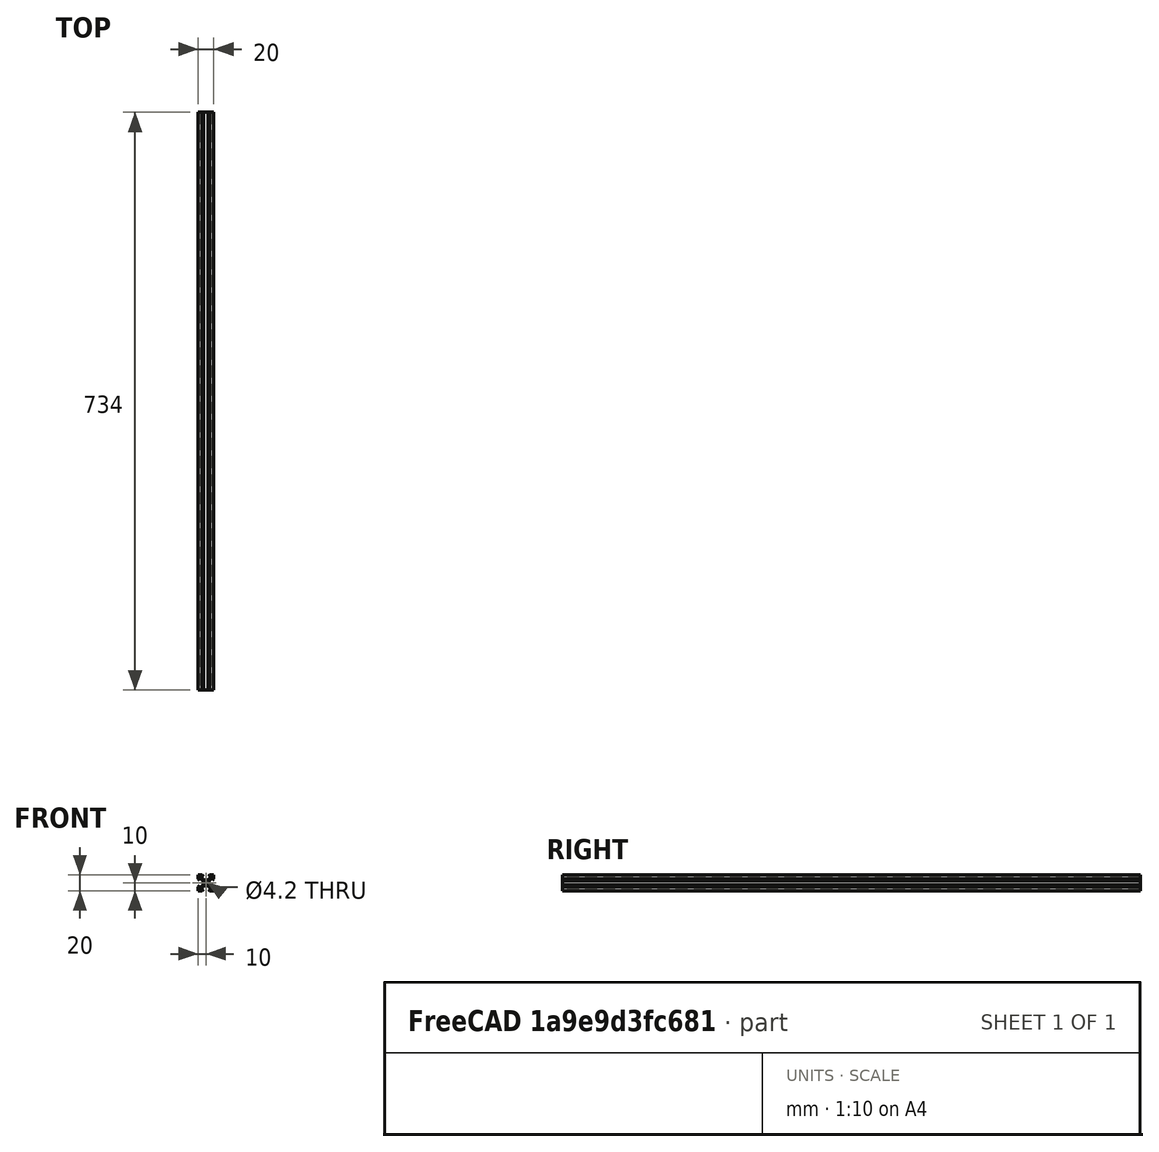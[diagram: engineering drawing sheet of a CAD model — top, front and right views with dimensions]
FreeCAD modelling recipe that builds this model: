
FCSTD DOCUMENT  (FreeCAD 0.20R29177 (Git))
Label: Vlot long
License: All rights reserved
LicenseURL: http://en.wikipedia.org/wiki/All_rights_reserved
objects: Sketcher::SketchObject×1, PartDesign::Pad×1, PartDesign::Body×1
note: 4 computed .brp shape members not serialized (recipe doc carries the construction recipe); baked Part::Feature solids carry a one-line shape summary decoded from their .brp

FEATURE [Sketcher::SketchObject] Sketch
  FullyConstrained = true
  MapMode = 5
  Placement = pos=(0,0,0) rot=(1,0,0;1.5708rad)
  Support = -> [XZ_Plane]
  sketch-geometry (43):
    g0: LineSegment StartX=0 StartY=0 StartZ=0 EndX=5.05 EndY=0 EndZ=0
    g1: LineSegment StartX=20 StartY=20 StartZ=0 EndX=14.95 EndY=20 EndZ=0
    g2: LineSegment StartX=0 StartY=20 StartZ=0 EndX=0 EndY=14.95 EndZ=0
    g3: LineSegment StartX=5.05 StartY=20 StartZ=0 EndX=6.9 EndY=18.15 EndZ=0
    g4: LineSegment StartX=6.9 StartY=18.15 StartZ=0 EndX=2.91066 EndY=18.15 EndZ=0
    g5: LineSegment StartX=2.91066 StartY=18.15 StartZ=0 EndX=7.16066 EndY=13.9 EndZ=0
    g6: LineSegment StartX=7.16066 StartY=13.9 StartZ=0 EndX=12.8393 EndY=13.9 EndZ=0
    g7: LineSegment StartX=12.8393 StartY=13.9 StartZ=0 EndX=17.0893 EndY=18.15 EndZ=0
    g8: LineSegment StartX=17.0893 StartY=18.15 StartZ=0 EndX=13.1 EndY=18.15 EndZ=0
    g9: LineSegment StartX=13.1 StartY=18.15 StartZ=0 EndX=14.95 EndY=20 EndZ=0
    g10: LineSegment StartX=0 StartY=20 StartZ=0 EndX=2.91066 EndY=18.15 EndZ=0
    g11: LineSegment StartX=17.0893 StartY=18.15 StartZ=0 EndX=20 EndY=20 EndZ=0
    g12: LineSegment StartX=0 StartY=20 StartZ=0 EndX=20 EndY=0 EndZ=0
    g13: LineSegment StartX=5.05 StartY=20 StartZ=0 EndX=0 EndY=20 EndZ=0
    g14: LineSegment StartX=0 StartY=20 StartZ=0 EndX=20 EndY=20 EndZ=0
    g15: LineSegment StartX=20 StartY=14.95 StartZ=0 EndX=18.15 EndY=13.1 EndZ=0
    g16: LineSegment StartX=18.15 StartY=13.1 StartZ=0 EndX=18.15 EndY=17.0893 EndZ=0
    g17: LineSegment StartX=18.15 StartY=17.0893 StartZ=0 EndX=13.9 EndY=12.8393 EndZ=0
    g18: LineSegment StartX=13.9 StartY=12.8393 StartZ=0 EndX=13.9 EndY=7.16066 EndZ=0
    g19: LineSegment StartX=13.9 StartY=7.16066 StartZ=0 EndX=18.15 EndY=2.91066 EndZ=0
    g20: LineSegment StartX=20 StartY=14.95 StartZ=0 EndX=20 EndY=20 EndZ=0
    g21: LineSegment StartX=18.15 StartY=2.91066 StartZ=0 EndX=18.15 EndY=6.9 EndZ=0
    g22: LineSegment StartX=18.15 StartY=6.9 StartZ=0 EndX=20 EndY=5.05 EndZ=0
    g23: LineSegment StartX=20 StartY=5.05 StartZ=0 EndX=20 EndY=0 EndZ=0
    g24: LineSegment StartX=5.05 StartY=0 StartZ=0 EndX=6.9 EndY=1.85 EndZ=0
    g25: LineSegment StartX=6.9 StartY=1.85 StartZ=0 EndX=2.91066 EndY=1.85 EndZ=0
    g26: LineSegment StartX=2.91066 StartY=1.85 StartZ=0 EndX=7.16066 EndY=6.1 EndZ=0
    g27: LineSegment StartX=7.16066 StartY=6.1 StartZ=0 EndX=12.8393 EndY=6.1 EndZ=0
    g28: LineSegment StartX=12.8393 StartY=6.1 StartZ=0 EndX=17.0893 EndY=1.85 EndZ=0
    g29: LineSegment StartX=17.0893 StartY=1.85 StartZ=0 EndX=13.1 EndY=1.85 EndZ=0
    g30: LineSegment StartX=13.1 StartY=1.85 StartZ=0 EndX=14.95 EndY=0 EndZ=0
    g31: LineSegment StartX=14.95 StartY=0 StartZ=0 EndX=20 EndY=0 EndZ=0
    g32: LineSegment StartX=0 StartY=14.95 StartZ=0 EndX=1.85 EndY=13.1 EndZ=0
    g33: LineSegment StartX=1.85 StartY=13.1 StartZ=0 EndX=1.85 EndY=17.0893 EndZ=0
    g34: LineSegment StartX=1.85 StartY=17.0893 StartZ=0 EndX=6.1 EndY=12.8393 EndZ=0
    g35: LineSegment StartX=6.1 StartY=12.8393 StartZ=0 EndX=6.1 EndY=7.16066 EndZ=0
    g36: LineSegment StartX=6.1 StartY=7.16066 StartZ=0 EndX=1.85 EndY=2.91066 EndZ=0
    g37: LineSegment StartX=1.85 StartY=2.91066 StartZ=0 EndX=1.85 EndY=6.9 EndZ=0
    g38: LineSegment StartX=1.85 StartY=6.9 StartZ=0 EndX=-2e-16 EndY=5.05 EndZ=0
    g39: LineSegment StartX=-2e-16 StartY=5.05 StartZ=0 EndX=0 EndY=0 EndZ=0
    g40: LineSegment StartX=0 StartY=20 StartZ=0 EndX=0 EndY=0 EndZ=0
    g41: LineSegment StartX=0 StartY=0 StartZ=0 EndX=10 EndY=10 EndZ=0
    g42: Circle CenterX=10 CenterY=10 CenterZ=0 NormalX=0 NormalY=0 NormalZ=1 AngleXU=0 Radius=2.1
  constraints (119):
    c: Coincident(g20,g1)
    c: Coincident(g13,g2)
    c: Coincident(g39,g0)
    c: Horizontal(g0)
    c: Horizontal(g1)
    c: Vertical(g2)
    c: Coincident(g0,g-1)
    c: DistanceY(g39,g2) = 20
    c: Coincident(g4,g3)
    c: Horizontal(g4)
    c: Coincident(g6,g5)
    c: Horizontal(g6)
    c: Coincident(g8,g7)
    c: Horizontal(g8)
    c: Coincident(g9,g8)
    c: Equal(g3,g9)
    c: Equal(g8,g4)
    c: Equal(g5,g7)
    c: Coincident(g4,g5)
    c: PointOnObject(g3,g8)
    c: Coincident(g7,g6)
    c: Coincident(g10,g13)
    c: Coincident(g10,g4)
    c: Coincident(g11,g7)
    c: Coincident(g11,g20)
    c: Equal(g10,g11)
    c: Coincident(g12,g13)
    c: Coincident(g12,g31)
    c: Parallel(g5,g12)
    c: Parallel(g3,g5)
    c: DistanceY(g3,g3) = 1.85
    c: DistanceY(g5,g3) = 6.1
    c: DistanceX(g3,g8) = 6.2
    c: Distance(g5,g12) = 0.75
    c: Coincident(g1,g9)
    c: Coincident(g13,g3)
    c: Tangent(g1,g13)
    c: Coincident(g14,g2)
    c: Coincident(g14,g20)
    c: Coincident(g16,g15)
    c: Coincident(g17,g16)
    c: Coincident(g18,g17)
    c: Vertical(g18)
    c: Coincident(g19,g18)
    c: Coincident(g20,g15)
    c: Equal(g9,g15)
    c: Vertical(g16)
    c: Equal(g17,g19)
    c: Parallel(g7,g17)
    c: Parallel(g17,g15)
    c: Parallel(g19,g12)
    c: Equal(g17,g7)
    c: Equal(g18,g6)
    c: Vertical(g20)
    c: Equal(g16,g8)
    c: Equal(g1,g20)
    c: Coincident(g21,g19)
    c: Vertical(g21)
    c: Coincident(g22,g21)
    c: Coincident(g23,g22)
    c: Coincident(g23,g31)
    c: Equal(g16,g21)
    c: Equal(g22,g15)
    c: Equal(g23,g20)
    c: Coincident(g25,g24)
    c: Horizontal(g25)
    c: Coincident(g26,g25)
    c: Horizontal(g27)
    c: Coincident(g29,g28)
    c: Horizontal(g29)
    c: Coincident(g30,g29)
    c: Equal(g24,g30)
    c: Equal(g29,g25)
    c: Equal(g26,g28)
    c: Coincident(g28,g27)
    c: Coincident(g27,g26)
    c: Parallel(g28,g12)
    c: Parallel(g24,g26)
    c: Parallel(g26,g17)
    c: Equal(g30,g22)
    c: Equal(g28,g19)
    c: Equal(g27,g18)
    c: Equal(g29,g21)
    c: Coincident(g0,g24)
    c: Coincident(g31,g30)
    c: Tangent(g0,g31)
    c: Vertical(g23)
    c: Equal(g23,g31)
    c: Coincident(g33,g32)
    c: Vertical(g33)
    c: Coincident(g34,g33)
    c: Coincident(g35,g34)
    c: Vertical(g35)
    c: Coincident(g36,g35)
    c: Coincident(g37,g36)
    c: Vertical(g37)
    c: Coincident(g38,g37)
    c: Coincident(g2,g32)
    c: Coincident(g39,g38)
    c: Tangent(g2,g39)
    c: Equal(g32,g38)
    c: Equal(g36,g34)
    c: Equal(g35,g27)
    c: Equal(g26,g36)
    c: Equal(g38,g24)
    c: Equal(g0,g39)
    c: Parallel(g38,g36)
    c: Parallel(g38,g26)
    c: Parallel(g34,g32)
    c: Equal(g2,g13)
    c: Equal(g33,g4)
    c: Coincident(g40,g2)
    c: Coincident(g40,g0)
    c: Equal(g14,g40)
    c: Coincident(g41,g0)
    c: PointOnObject(g41,g12)
    c: Perpendicular(g12,g41)
    c: Coincident(g42,g41)
    c: Diameter(g42) = 4.2
FEATURE [PartDesign::Pad] Pad
  Direction = (1,1,1)
  Length = 734
  Length2 = 100
  Placement = pos=(0,0,0) rot=(1,0,0;1.5708rad)
  Profile = -> Sketch
  Type = 0
FEATURE [PartDesign::Body] Body  label="Vslot 1"
  Group = -> [Sketch,Pad]
  Origin = -> Origin
  Tip = -> Pad
